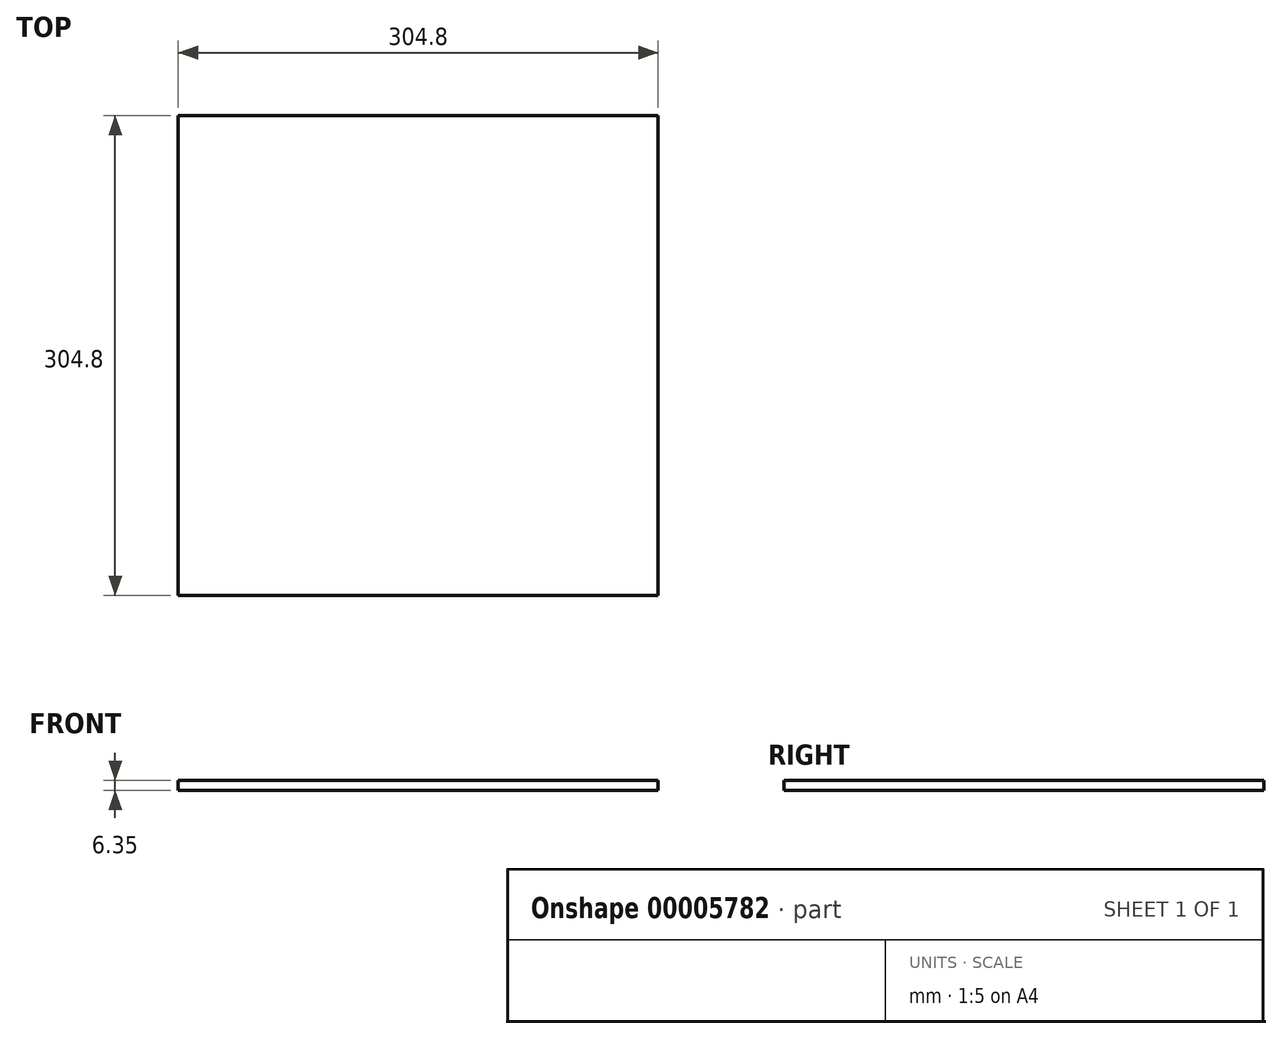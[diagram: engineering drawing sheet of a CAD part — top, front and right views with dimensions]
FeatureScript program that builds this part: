
annotation { "Feature Type Name" : "Feature", "Feature Type Description" : "" }
export const myFeature = defineFeature(function(context is Context, id is Id, definition is map)
    precondition{}
    {
        {
            var Q0;
            Q0=qCreatedBy(makeId("Top.planeOp"),FACE);
            var sketch = newSketch(context, id + "F0", { "sketchPlane" : qUnion([Q0])});
            skLineSegment(sketch, "E0.bottom", {"start": v(0, 0) * mm, "end": v(304.8, 0) * mm});
            skLineSegment(sketch, "E0.top", {"start": v(0, 304.8) * mm, "end": v(304.8, 304.8) * mm});
            skLineSegment(sketch, "E0.left", {"start": v(0, 0) * mm, "end": v(0, 304.8) * mm});
            skLineSegment(sketch, "E0.right", {"start": v(304.8, 0) * mm, "end": v(304.8, 304.8) * mm});
            skSolve(sketch);
        }
        {
            var Q0;
            Q0=makeQuery(id+"F0.imprint","IMPRINT",FACE,{"disambiguationData":[TD([[makeQuery(id+"F0.imprint","IMPRINT",EDGE,{"derivedFrom":sQuery(id+"F0.wireOp",EDGE,"E0.bottom")}),1.0]])]});
            extrude(context, id + "F1", {"entities" : qUnion([Q0]), "depth" : 6.35 * mm});
        }
    });
